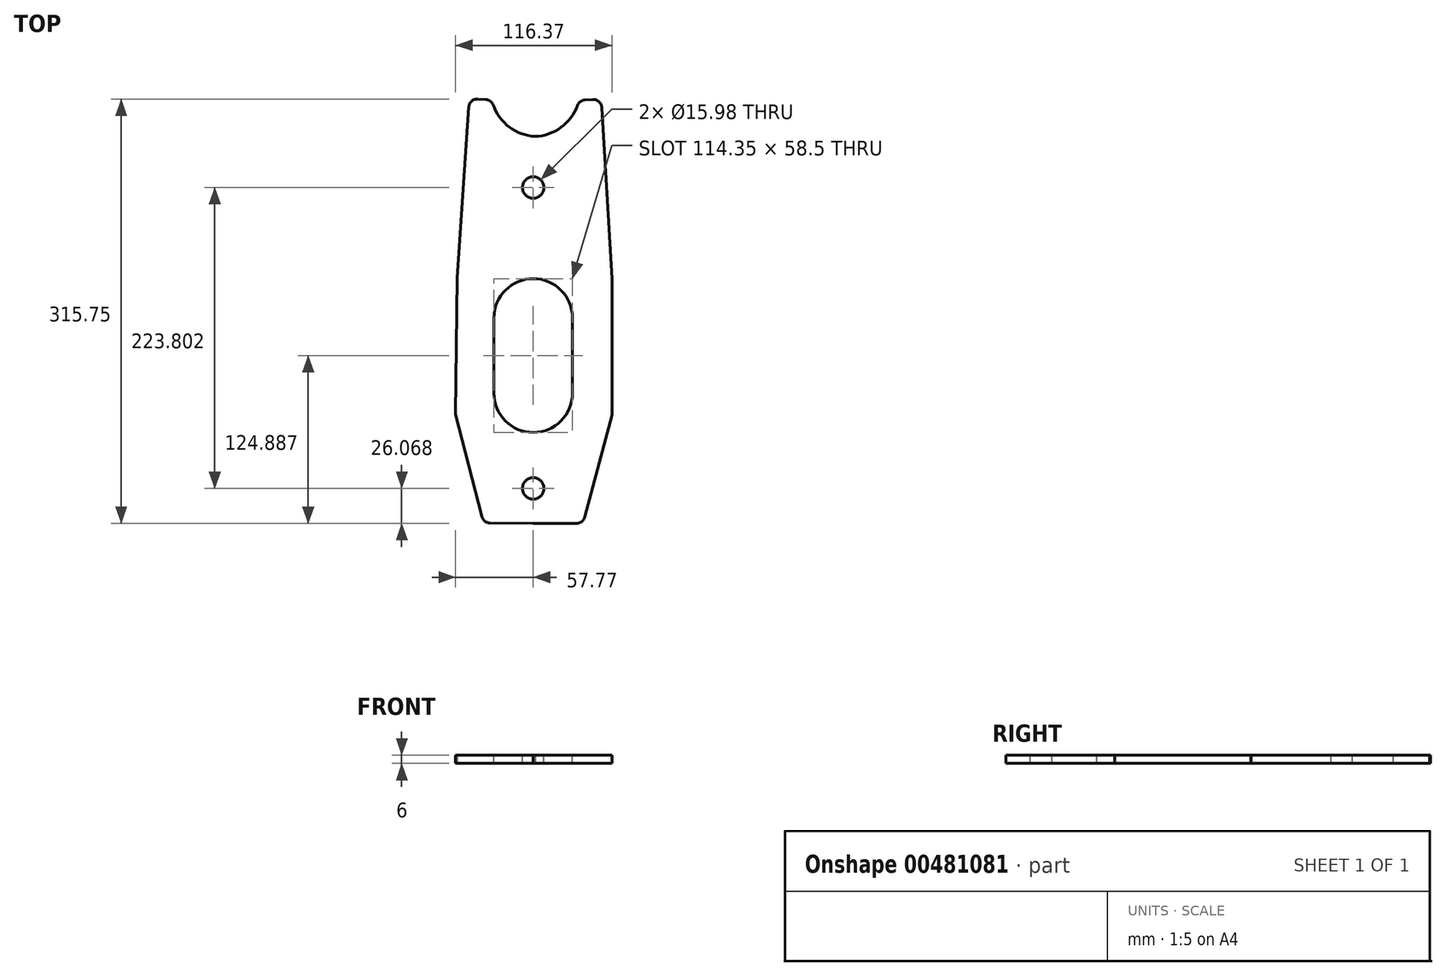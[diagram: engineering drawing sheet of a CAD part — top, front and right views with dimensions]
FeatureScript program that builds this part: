
annotation { "Feature Type Name" : "Feature", "Feature Type Description" : "" }
export const myFeature = defineFeature(function(context is Context, id is Id, definition is map)
    precondition{}
    {
        {
            var Q0;
            Q0=qCreatedBy(makeId("Top.planeOp"),FACE);
            var sketch = newSketch(context, id + "F0", { "sketchPlane" : qUnion([Q0])});
            skLineSegment(sketch, "E0", {"start": v(0, 0) * mm, "end": v(36.98, 0) * mm});
            skLineSegment(sketch, "E1", {"start": v(36.98, 0) * mm, "end": v(58.6, 0) * mm, "construction": true});
            skLineSegment(sketch, "E2", {"start": v(58.6, 0) * mm, "end": v(58.6, 80.74) * mm, "construction": true});
            skLineSegment(sketch, "E3", {"start": v(58.6, 80.74) * mm, "end": v(36.98, 0) * mm});
            skLineSegment(sketch, "E4", {"start": v(58.6, 80.74) * mm, "end": v(58.6, 182.06) * mm});
            skLineSegment(sketch, "E5", {"start": v(58.6, 182.06) * mm, "end": v(58.6, 315.68) * mm, "construction": true});
            skLineSegment(sketch, "E6", {"start": v(58.6, 315.68) * mm, "end": v(50.69, 315.68) * mm, "construction": true});
            skLineSegment(sketch, "E7", {"start": v(50.69, 315.68) * mm, "end": v(58.6, 182.06) * mm});
            skLineSegment(sketch, "E8", {"start": v(50.69, 315.68) * mm, "end": v(0, 312.67) * mm, "construction": true});
            skLineSegment(sketch, "E9", {"start": v(0, 312.67) * mm, "end": v(1.47, 287.85) * mm, "construction": true});
            skLineSegment(sketch, "E10", {"start": v(1.47, 287.85) * mm, "end": v(0, 322.82) * mm, "construction": true});
            skArc(sketch, "E11", {"start": v(1.47, 287.85) * mm, "mid": v(22.26, 295.8) * mm, "end": v(34.04, 314.7) * mm});
            skLineSegment(sketch, "E12", {"start": v(34.04, 314.7) * mm, "end": v(50.69, 315.68) * mm});
            skLineSegment(sketch, "E13", {"start": v(1.47, 287.85) * mm, "end": v(0, 0) * mm});
            skArc(sketch, "E14.MirrorCS", {"start": v(1.47, 287.85) * mm, "mid": v(-19.24, 296.02) * mm, "end": v(-30.83, 315.02) * mm});
            skLineSegment(sketch, "E15.MirrorCS", {"start": v(-47.46, 316.18) * mm, "end": v(3.2, 312.66) * mm, "construction": true});
            skLineSegment(sketch, "E16.MirrorCS", {"start": v(-47.46, 316.18) * mm, "end": v(-56.74, 182.65) * mm});
            skLineSegment(sketch, "E17.MirrorCS", {"start": v(-57.77, 81.33) * mm, "end": v(-56.74, 182.65) * mm});
            skLineSegment(sketch, "E18.MirrorCS", {"start": v(-57.77, 81.33) * mm, "end": v(-36.98, 0.38) * mm});
            skLineSegment(sketch, "E19.MirrorCS", {"start": v(0, 0) * mm, "end": v(-36.98, 0.38) * mm});
            skLineSegment(sketch, "E20", {"start": v(-47.46, 316.18) * mm, "end": v(-30.83, 315.02) * mm});
            skSolve(sketch);
        }
        {
            var Q0;
            Q0=qSketchRegion(id+"F0",true);
            extrude(context, id + "F1", {"entities" : qUnion([Q0]), "depth" : 6 * mm});
        }
        {
            var Q0;
            Q0=makeQuery(id+"F1.opExtrude","CAP_FACE",FACE,{"disambiguationData":[OSD([sQuery(id+"F0.wireOp",EDGE,"E0"),sQuery(id+"F0.wireOp",EDGE,"E3"),sQuery(id+"F0.wireOp",EDGE,"E4"),sQuery(id+"F0.wireOp",EDGE,"E7"),sQuery(id+"F0.wireOp",EDGE,"E11"),sQuery(id+"F0.wireOp",EDGE,"E12"),sQuery(id+"F0.wireOp",EDGE,"E14.MirrorCS"),sQuery(id+"F0.wireOp",EDGE,"E16.MirrorCS"),sQuery(id+"F0.wireOp",EDGE,"E17.MirrorCS"),sQuery(id+"F0.wireOp",EDGE,"E18.MirrorCS"),sQuery(id+"F0.wireOp",EDGE,"E19.MirrorCS"),sQuery(id+"F0.wireOp",EDGE,"E20")])],"isStart":false});
            var sketch = newSketch(context, id + "F2", { "sketchPlane" : qUnion([Q0])});
            skLineSegment(sketch, "E21", {"start": v(0, 0) * mm, "end": v(0, 26.07) * mm, "construction": true});
            skLineSegment(sketch, "E22", {"start": v(0, 26.07) * mm, "end": v(0, 249.87) * mm, "construction": true});
            skCircle(sketch, "E23", {"center": v(0, 249.87) * mm, "radius": 7.99 * mm});
            skCircle(sketch, "E24", {"center": v(0, 26.07) * mm, "radius": 7.99 * mm});
            skSolve(sketch);
        }
        {
            var Q0;
            Q0=qSketchRegion(id+"F2",true);
            extrude(context, id + "F3", {"entities" : qUnion([Q0]), "operationType" : NewBodyOperationType.REMOVE, "oppositeDirection" : true, "depth" : 25.4 * mm});
        }
        {
            var Q0;
            Q0=makeQuery(id+"F1.opExtrude","CAP_FACE",FACE,{"disambiguationData":[OSD([sQuery(id+"F0.wireOp",EDGE,"E0"),sQuery(id+"F0.wireOp",EDGE,"E3"),sQuery(id+"F0.wireOp",EDGE,"E4"),sQuery(id+"F0.wireOp",EDGE,"E7"),sQuery(id+"F0.wireOp",EDGE,"E11"),sQuery(id+"F0.wireOp",EDGE,"E12"),sQuery(id+"F0.wireOp",EDGE,"E14.MirrorCS"),sQuery(id+"F0.wireOp",EDGE,"E16.MirrorCS"),sQuery(id+"F0.wireOp",EDGE,"E17.MirrorCS"),sQuery(id+"F0.wireOp",EDGE,"E18.MirrorCS"),sQuery(id+"F0.wireOp",EDGE,"E19.MirrorCS"),sQuery(id+"F0.wireOp",EDGE,"E20")])],"isStart":false});
            var sketch = newSketch(context, id + "F4", { "sketchPlane" : qUnion([Q0])});
            skSolve(sketch);
        }
        {
            var Q0;
            Q0=makeQuery(id+"F4.imprint","IMPRINT",FACE,{"disambiguationData":[TD([[makeQuery(id+"F4.imprint","IMPRINT",EDGE,{"derivedFrom":makeQuery(id+"F1.opExtrude","CAP_EDGE",EDGE,{"disambiguationData":[OSD([sQuery(id+"F0.wireOp",EDGE,"E0")])],"isStart":false})}),1.0]])]});
            var sketch = newSketch(context, id + "F5", { "sketchPlane" : qUnion([Q0])});
            skLineSegment(sketch, "E25", {"start": v(0, 0) * mm, "end": v(0, 182.06) * mm, "construction": true});
            skLineSegment(sketch, "E26", {"start": v(0, 182.06) * mm, "end": v(0, 67.71) * mm, "construction": true});
            skLineSegment(sketch, "E27", {"start": v(0, 67.71) * mm, "end": v(0, 96.96) * mm, "construction": true});
            skLineSegment(sketch, "E28", {"start": v(0, 96.96) * mm, "end": v(29.25, 96.96) * mm, "construction": true});
            skArc(sketch, "E29", {"start": v(0, 67.71) * mm, "mid": v(20.68, 76.28) * mm, "end": v(29.25, 96.96) * mm});
            skArc(sketch, "E30", {"start": v(0, 67.71) * mm, "mid": v(-20.68, 76.28) * mm, "end": v(-29.25, 96.96) * mm});
            skLineSegment(sketch, "E31", {"start": v(0, 182.06) * mm, "end": v(0, 152.81) * mm, "construction": true});
            skArc(sketch, "E32", {"start": v(0, 182.06) * mm, "mid": v(20.68, 173.5) * mm, "end": v(29.25, 152.81) * mm});
            skArc(sketch, "E33", {"start": v(0, 182.06) * mm, "mid": v(-20.68, 173.5) * mm, "end": v(-29.25, 152.81) * mm});
            skLineSegment(sketch, "E34", {"start": v(-29.25, 152.81) * mm, "end": v(-29.25, 96.96) * mm});
            skLineSegment(sketch, "E35", {"start": v(29.25, 152.81) * mm, "end": v(29.25, 96.96) * mm});
            skSolve(sketch);
        }
        {
            var Q0;
            Q0=qSketchRegion(id+"F5",true);
            extrude(context, id + "F6", {"entities" : qUnion([Q0]), "operationType" : NewBodyOperationType.REMOVE, "oppositeDirection" : true, "depth" : 25.4 * mm});
        }
        {
            var Q0;
            Q0=makeQuery(id+"F1.opExtrude","SWEPT_EDGE",EDGE,{"disambiguationData":[OSD([sQuery(id+"F0.wireOp",EDGE,"E18.MirrorCS"),sQuery(id+"F0.wireOp",EDGE,"E19.MirrorCS")])]});
            var Q1;
            Q1=makeQuery(id+"F1.opExtrude","SWEPT_EDGE",EDGE,{"disambiguationData":[OSD([sQuery(id+"F0.wireOp",EDGE,"E0"),sQuery(id+"F0.wireOp",EDGE,"E3")])]});
            var Q2;
            Q2=makeQuery(id+"F1.opExtrude","SWEPT_EDGE",EDGE,{"disambiguationData":[OSD([sQuery(id+"F0.wireOp",EDGE,"E7"),sQuery(id+"F0.wireOp",EDGE,"E12")])]});
            var Q3;
            Q3=makeQuery(id+"F1.opExtrude","SWEPT_EDGE",EDGE,{"disambiguationData":[OSD([sQuery(id+"F0.wireOp",EDGE,"E11"),sQuery(id+"F0.wireOp",EDGE,"E12")])]});
            var Q4;
            Q4=makeQuery(id+"F1.opExtrude","SWEPT_EDGE",EDGE,{"disambiguationData":[OSD([sQuery(id+"F0.wireOp",EDGE,"E14.MirrorCS"),sQuery(id+"F0.wireOp",EDGE,"E20")])]});
            var Q5;
            Q5=makeQuery(id+"F1.opExtrude","SWEPT_EDGE",EDGE,{"disambiguationData":[OSD([sQuery(id+"F0.wireOp",EDGE,"E16.MirrorCS"),sQuery(id+"F0.wireOp",EDGE,"E20")])]});
            fillet(context, id + "F7", {"entities" : qUnion([Q0, Q1, Q2, Q3, Q4, Q5]), "radius" : 6.35 * mm, "tangentPropagation" : true, "allowEdgeOverflow" : false});
        }
    });
